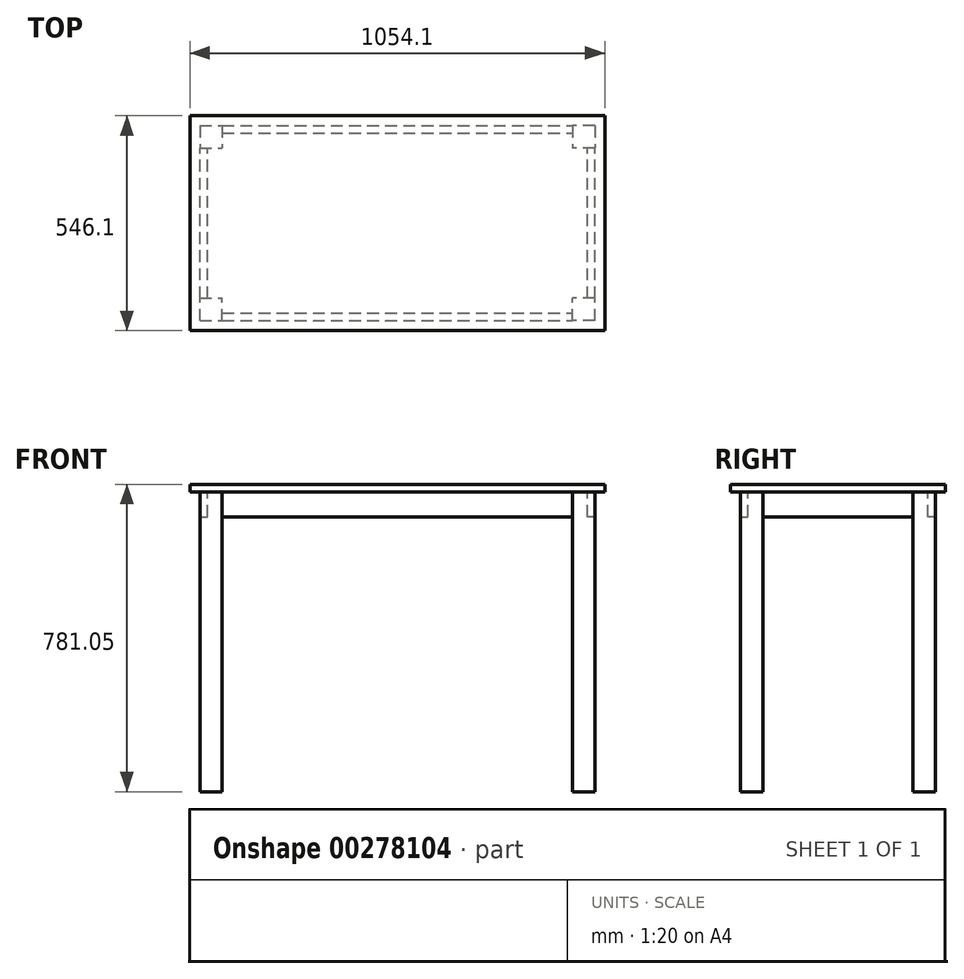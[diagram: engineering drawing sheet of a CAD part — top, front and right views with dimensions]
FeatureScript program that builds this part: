
annotation { "Feature Type Name" : "Feature", "Feature Type Description" : "" }
export const myFeature = defineFeature(function(context is Context, id is Id, definition is map)
    precondition{}
    {
        {
            var Q0;
            Q0=qCreatedBy(makeId("Top.planeOp"),FACE);
            var sketch = newSketch(context, id + "F0", { "sketchPlane" : qUnion([Q0])});
            skLineSegment(sketch, "E0.bottom", {"start": v(527.05, 273.05) * mm, "end": v(-527.05, 273.05) * mm});
            skLineSegment(sketch, "E0.top", {"start": v(527.05, -273.05) * mm, "end": v(-527.05, -273.05) * mm});
            skLineSegment(sketch, "E0.left", {"start": v(527.05, 273.05) * mm, "end": v(527.05, -273.05) * mm});
            skLineSegment(sketch, "E0.right", {"start": v(-527.05, 273.05) * mm, "end": v(-527.05, -273.05) * mm});
            skPoint(sketch, "E0.middle", {"position": v(0, 0) * mm});
            skSolve(sketch);
        }
        {
            var Q0;
            Q0=makeQuery(id+"F0.imprint","IMPRINT",FACE,{"disambiguationData":[TD([[makeQuery(id+"F0.imprint","IMPRINT",EDGE,{"derivedFrom":sQuery(id+"F0.wireOp",EDGE,"E0.bottom")}),1.0]])]});
            extrude(context, id + "F1", {"entities" : qUnion([Q0]), "depth" : 19.05 * mm});
        }
        {
            var Q0;
            Q0=makeQuery(id+"F1.opExtrude","CAP_FACE",FACE,{"disambiguationData":[OSD([sQuery(id+"F0.wireOp",EDGE,"E0.bottom"),sQuery(id+"F0.wireOp",EDGE,"E0.top"),sQuery(id+"F0.wireOp",EDGE,"E0.left"),sQuery(id+"F0.wireOp",EDGE,"E0.right")])],"isStart":true});
            var sketch = newSketch(context, id + "F2", { "sketchPlane" : qUnion([Q0])});
            skLineSegment(sketch, "E1.bottom", {"start": v(-501.65, 247.65) * mm, "end": v(-444.5, 247.65) * mm});
            skLineSegment(sketch, "E1.top", {"start": v(-501.65, 190.5) * mm, "end": v(-444.5, 190.5) * mm});
            skLineSegment(sketch, "E1.left", {"start": v(-501.65, 247.65) * mm, "end": v(-501.65, 190.5) * mm});
            skLineSegment(sketch, "E1.right", {"start": v(-444.5, 247.65) * mm, "end": v(-444.5, 190.5) * mm});
            skLineSegment(sketch, "E2.MirrorCS", {"start": v(501.65, 247.65) * mm, "end": v(444.5, 247.65) * mm});
            skLineSegment(sketch, "E3.MirrorCS", {"start": v(501.65, 190.5) * mm, "end": v(444.5, 190.5) * mm});
            skLineSegment(sketch, "E4.MirrorCS", {"start": v(501.65, 247.65) * mm, "end": v(501.65, 190.5) * mm});
            skLineSegment(sketch, "E5.MirrorCS", {"start": v(444.5, 247.65) * mm, "end": v(444.5, 190.5) * mm});
            skLineSegment(sketch, "E6.MirrorCS", {"start": v(501.65, -247.65) * mm, "end": v(501.65, -190.5) * mm});
            skLineSegment(sketch, "E7.MirrorCS", {"start": v(501.65, -190.5) * mm, "end": v(444.5, -190.5) * mm});
            skLineSegment(sketch, "E8.MirrorCS", {"start": v(501.65, -247.65) * mm, "end": v(444.5, -247.65) * mm});
            skLineSegment(sketch, "E9.MirrorCS", {"start": v(-444.5, -247.65) * mm, "end": v(-444.5, -190.5) * mm});
            skLineSegment(sketch, "E10.MirrorCS", {"start": v(-501.65, -247.65) * mm, "end": v(-501.65, -190.5) * mm});
            skLineSegment(sketch, "E11.MirrorCS", {"start": v(-501.65, -190.5) * mm, "end": v(-444.5, -190.5) * mm});
            skLineSegment(sketch, "E12.MirrorCS", {"start": v(-501.65, -247.65) * mm, "end": v(-444.5, -247.65) * mm});
            skLineSegment(sketch, "E13.MirrorCS", {"start": v(444.5, -247.65) * mm, "end": v(444.5, -190.5) * mm});
            skSolve(sketch);
        }
        {
            var Q0;
            Q0=makeQuery(id+"F2.imprint","IMPRINT",FACE,{"disambiguationData":[TD([[makeQuery(id+"F2.imprint","IMPRINT",EDGE,{"derivedFrom":sQuery(id+"F2.wireOp",EDGE,"E1.bottom")}),-1.0]])]});
            var Q1;
            Q1=makeQuery(id+"F2.imprint","IMPRINT",FACE,{"disambiguationData":[TD([[makeQuery(id+"F2.imprint","IMPRINT",EDGE,{"derivedFrom":sQuery(id+"F2.wireOp",EDGE,"E2.MirrorCS")}),1.0]])]});
            var Q2;
            Q2=makeQuery(id+"F2.imprint","IMPRINT",FACE,{"disambiguationData":[TD([[makeQuery(id+"F2.imprint","IMPRINT",EDGE,{"derivedFrom":sQuery(id+"F2.wireOp",EDGE,"E6.MirrorCS")}),1.0]])]});
            var Q3;
            Q3=makeQuery(id+"F2.imprint","IMPRINT",FACE,{"disambiguationData":[TD([[makeQuery(id+"F2.imprint","IMPRINT",EDGE,{"derivedFrom":sQuery(id+"F2.wireOp",EDGE,"E9.MirrorCS")}),1.0]])]});
            extrude(context, id + "F3", {"entities" : qUnion([Q0, Q1, Q2, Q3]), "depth" : 762 * mm});
        }
        {
            var Q0;
            Q0=makeQuery(id+"F1.opExtrude","CAP_FACE",FACE,{"disambiguationData":[OSD([sQuery(id+"F0.wireOp",EDGE,"E0.bottom"),sQuery(id+"F0.wireOp",EDGE,"E0.top"),sQuery(id+"F0.wireOp",EDGE,"E0.left"),sQuery(id+"F0.wireOp",EDGE,"E0.right")])],"isStart":true});
            var sketch = newSketch(context, id + "F4", { "sketchPlane" : qUnion([Q0])});
            skLineSegment(sketch, "E14.bottom", {"start": v(-444.5, 247.65) * mm, "end": v(444.5, 247.65) * mm});
            skLineSegment(sketch, "E14.top", {"start": v(-444.5, 228.6) * mm, "end": v(444.5, 228.6) * mm});
            skLineSegment(sketch, "E14.left", {"start": v(-444.5, 247.65) * mm, "end": v(-444.5, 228.6) * mm});
            skLineSegment(sketch, "E14.right", {"start": v(444.5, 247.65) * mm, "end": v(444.5, 228.6) * mm});
            skLineSegment(sketch, "E15.bottom", {"start": v(-501.65, 190.5) * mm, "end": v(-482.6, 190.5) * mm});
            skLineSegment(sketch, "E15.top", {"start": v(-501.65, -190.5) * mm, "end": v(-482.6, -190.5) * mm});
            skLineSegment(sketch, "E15.left", {"start": v(-501.65, 190.5) * mm, "end": v(-501.65, -190.5) * mm});
            skLineSegment(sketch, "E15.right", {"start": v(-482.6, 190.5) * mm, "end": v(-482.6, -190.5) * mm});
            skLineSegment(sketch, "E16.MirrorCS", {"start": v(-444.5, -247.65) * mm, "end": v(-444.5, -228.6) * mm});
            skLineSegment(sketch, "E17.MirrorCS", {"start": v(444.5, -247.65) * mm, "end": v(444.5, -228.6) * mm});
            skLineSegment(sketch, "E18.MirrorCS", {"start": v(-444.5, -247.65) * mm, "end": v(444.5, -247.65) * mm});
            skLineSegment(sketch, "E19.MirrorCS", {"start": v(-444.5, -228.6) * mm, "end": v(444.5, -228.6) * mm});
            skLineSegment(sketch, "E20.MirrorCS", {"start": v(501.65, -190.5) * mm, "end": v(482.6, -190.5) * mm});
            skLineSegment(sketch, "E21.MirrorCS", {"start": v(501.65, 190.5) * mm, "end": v(482.6, 190.5) * mm});
            skLineSegment(sketch, "E22.MirrorCS", {"start": v(482.6, 190.5) * mm, "end": v(482.6, -190.5) * mm});
            skLineSegment(sketch, "E23.MirrorCS", {"start": v(501.65, 190.5) * mm, "end": v(501.65, -190.5) * mm});
            skSolve(sketch);
        }
        {
            var Q0;
            Q0=makeQuery(id+"F4.imprint","IMPRINT",FACE,{"disambiguationData":[TD([[makeQuery(id+"F4.imprint","IMPRINT",EDGE,{"derivedFrom":sQuery(id+"F4.wireOp",EDGE,"E14.bottom")}),-1.0]])]});
            var Q1;
            Q1=makeQuery(id+"F4.imprint","IMPRINT",FACE,{"disambiguationData":[TD([[makeQuery(id+"F4.imprint","IMPRINT",EDGE,{"derivedFrom":sQuery(id+"F4.wireOp",EDGE,"E15.bottom")}),-1.0]])]});
            var Q2;
            Q2=makeQuery(id+"F4.imprint","IMPRINT",FACE,{"disambiguationData":[TD([[makeQuery(id+"F4.imprint","IMPRINT",EDGE,{"derivedFrom":sQuery(id+"F4.wireOp",EDGE,"E16.MirrorCS")}),-1.0]])]});
            var Q3;
            Q3=makeQuery(id+"F4.imprint","IMPRINT",FACE,{"disambiguationData":[TD([[makeQuery(id+"F4.imprint","IMPRINT",EDGE,{"derivedFrom":sQuery(id+"F4.wireOp",EDGE,"E20.MirrorCS")}),-1.0]])]});
            extrude(context, id + "F5", {"entities" : qUnion([Q0, Q1, Q2, Q3]), "depth" : 63.5 * mm});
        }
    });
